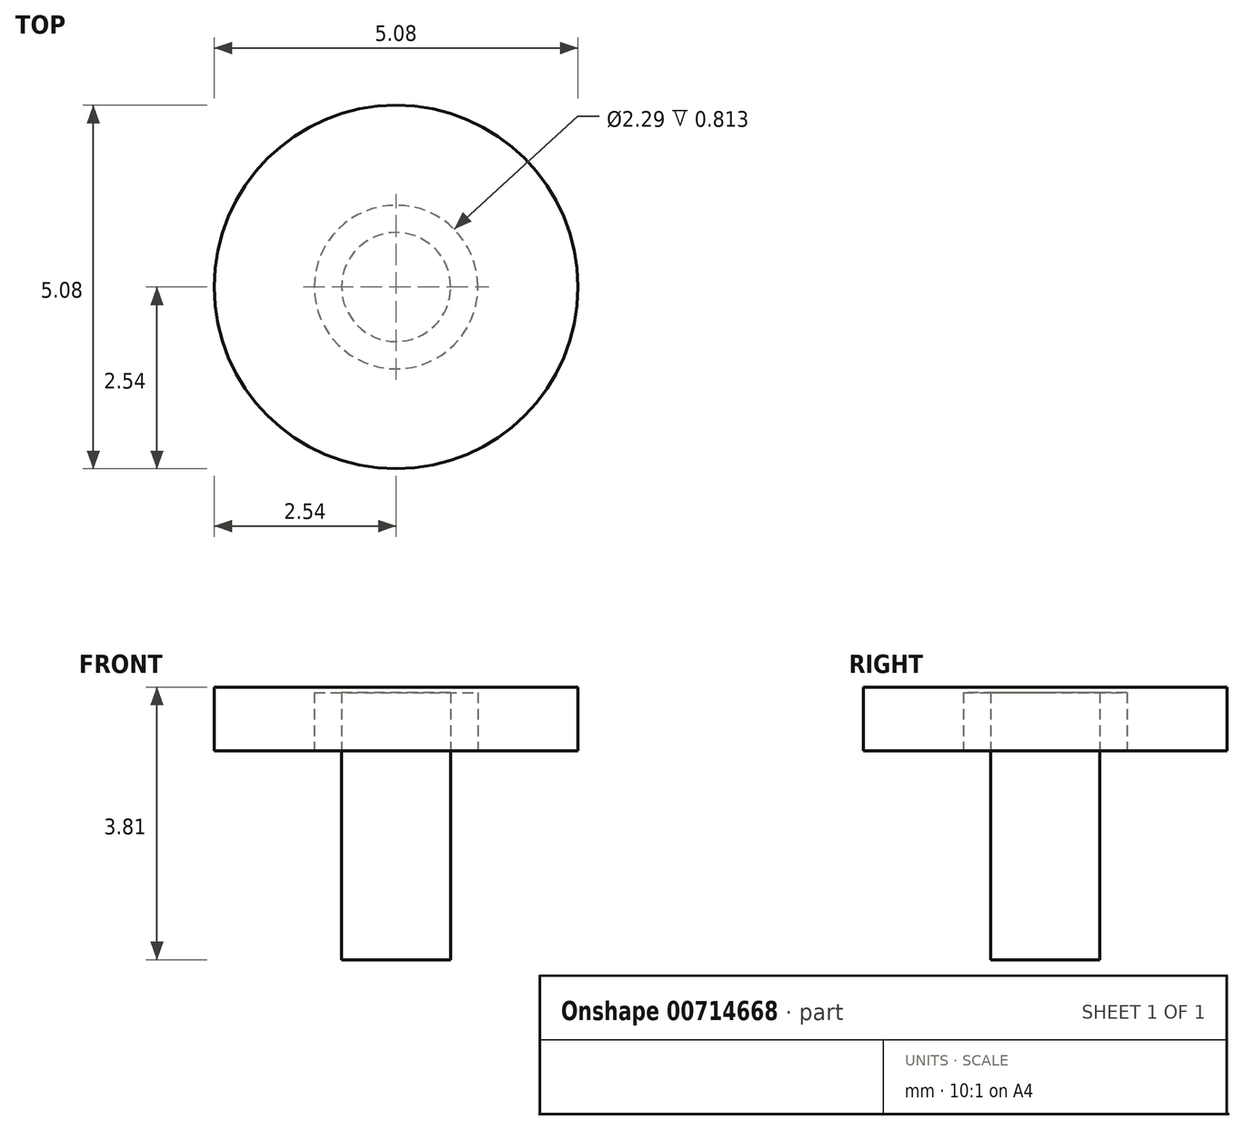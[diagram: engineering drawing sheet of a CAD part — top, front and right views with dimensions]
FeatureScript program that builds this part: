
annotation { "Feature Type Name" : "Feature", "Feature Type Description" : "" }
export const myFeature = defineFeature(function(context is Context, id is Id, definition is map)
    precondition{}
    {
        {
            var Q0;
            Q0=qCreatedBy(makeId("Top.planeOp"),FACE);
            var sketch = newSketch(context, id + "F0", { "sketchPlane" : qUnion([Q0])});
            skCircle(sketch, "E0", {"center": v(0, 0) * mm, "radius": 0.76 * mm});
            skSolve(sketch);
        }
        {
            var Q0;
            Q0 = qSketchRegion(id + "F0", true);
            extrude(context, id + "F1", {"entities" : qUnion([Q0]), "depth" : 3.8 * mm, "offsetDistance" : 25.4 * mm});
        }
        {
            var Q0;
            Q0=makeQuery(id+"F1.opExtrude","CAP_FACE",FACE,{"disambiguationData":[OSD([sQuery(id+"F0.wireOp",EDGE,"E0")])],"isStart":false});
            var sketch = newSketch(context, id + "F2", { "sketchPlane" : qUnion([Q0])});
            skCircle(sketch, "E1", {"center": v(0, 0) * mm, "radius": 2.54 * mm});
            skSolve(sketch);
        }
        {
            var Q0;
            Q0 = qSketchRegion(id + "F2", true);
            extrude(context, id + "F3", {"entities" : qUnion([Q0]), "operationType" : NewBodyOperationType.ADD, "oppositeDirection" : true, "depth" : 0.64 * mm, "offsetDistance" : 25.4 * mm});
        }
        {
            var Q0;
            Q0=makeQuery(id+"F3.opExtrude","CAP_FACE",FACE,{"disambiguationData":[OSD([sQuery(id+"F2.wireOp",EDGE,"E1")])],"isStart":false});
            var sketch = newSketch(context, id + "F4", { "sketchPlane" : qUnion([Q0])});
            skCircle(sketch, "E2", {"center": v(0, 0) * mm, "radius": 1.14 * mm});
            skSolve(sketch);
        }
        {
            var Q0;
            Q0=makeQuery(id+"F4.imprint","IMPRINT",FACE,{"disambiguationData":[TD([[makeQuery(id+"F4.imprint","IMPRINT",EDGE,{"derivedFrom":sQuery(id+"F4.wireOp",EDGE,"E2")}),1.0]])]});
            extrude(context, id + "F5", {"entities" : qUnion([Q0]), "operationType" : NewBodyOperationType.REMOVE, "oppositeDirection" : true, "depth" : 0.56 * mm, "offsetDistance" : 25.4 * mm});
        }
        {
            var Q0;
            Q0=makeQuery(id+"F3.opExtrude","CAP_FACE",FACE,{"disambiguationData":[OSD([sQuery(id+"F2.wireOp",EDGE,"E1")])],"isStart":false});
            extrude(context, id + "F6", {"entities" : qUnion([Q0]), "operationType" : NewBodyOperationType.ADD, "depth" : 0.25 * mm, "offsetDistance" : 25.4 * mm});
        }
    });
